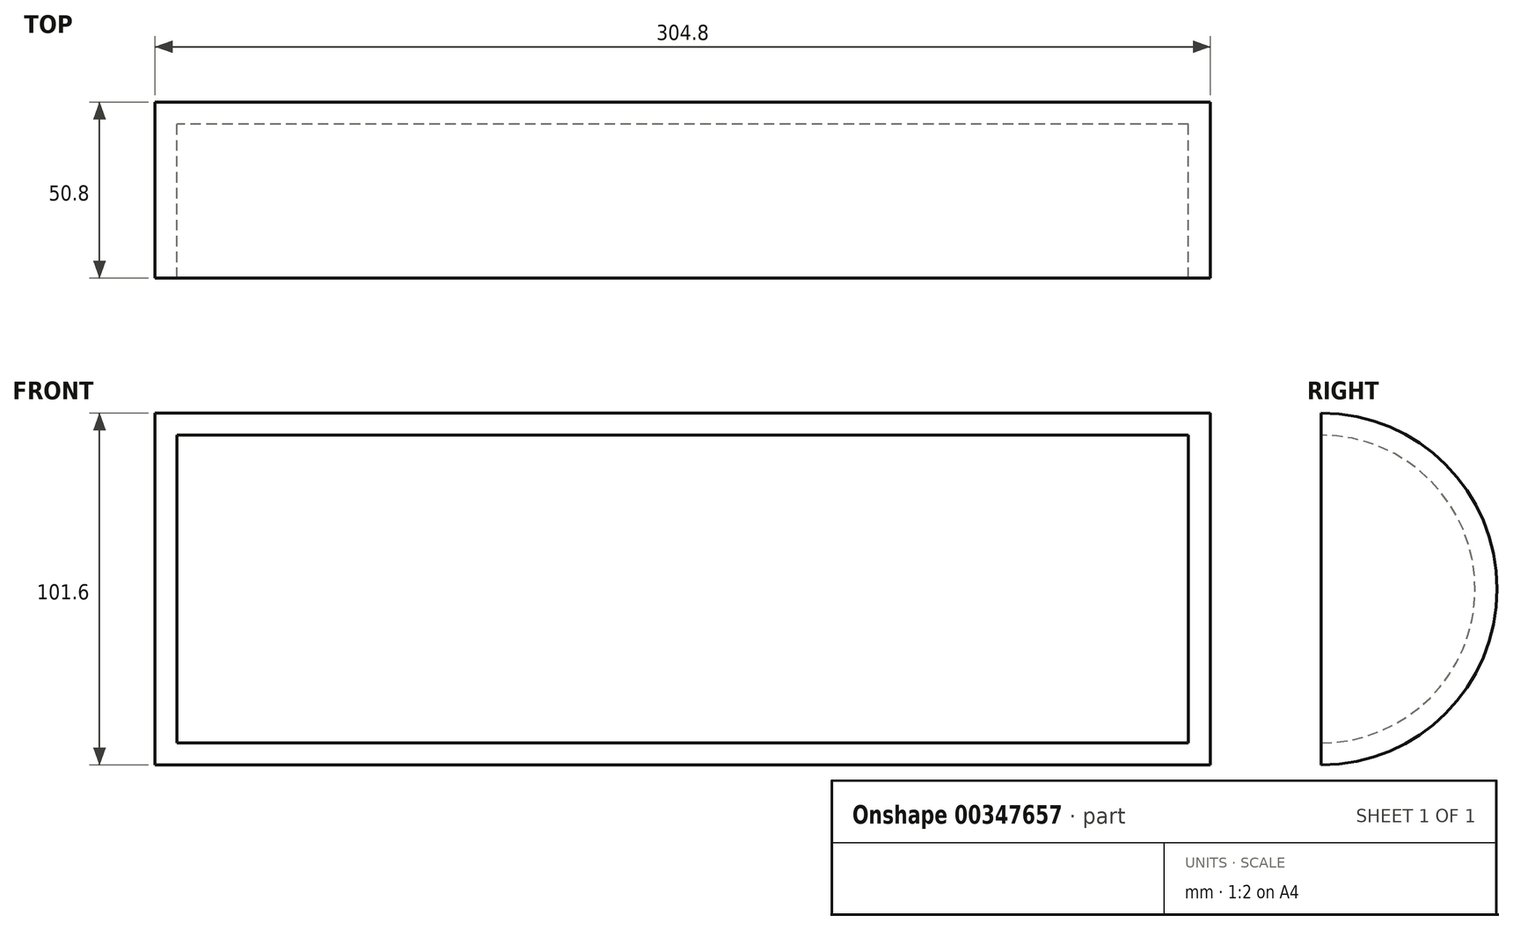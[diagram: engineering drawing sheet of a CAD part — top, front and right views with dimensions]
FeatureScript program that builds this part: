
annotation { "Feature Type Name" : "Feature", "Feature Type Description" : "" }
export const myFeature = defineFeature(function(context is Context, id is Id, definition is map)
    precondition{}
    {
        {
            var Q0;
            Q0=qCreatedBy(makeId("Right.planeOp"),FACE);
            var sketch = newSketch(context, id + "F0", { "sketchPlane" : qUnion([Q0])});
            skCircle(sketch, "E0", {"center": v(0, 0) * mm, "radius": 50.8 * mm});
            skLineSegment(sketch, "E1", {"start": v(0, 50.8) * mm, "end": v(0, -50.8) * mm});
            skSolve(sketch);
        }
        {
            var Q0;
            {var subQ0=sQuery(id+"F0.wireOp",EDGE,"E1");Q0=makeQuery(id+"F0.imprint","IMPRINT",FACE,{"disambiguationData":[TD([[makeQuery(id+"F0.imprint","IMPRINT",EDGE,{"derivedFrom":subQ0}),1.0]])]});}
            extrude(context, id + "F1", {"entities" : qUnion([Q0]), "depth" : 304.8 * mm, "hasSecondDirection" : true, "secondDirectionOppositeDirection" : true, "secondDirectionDepth" : 76.2 * mm, "symmetric" : true});
        }
        {
            var Q0;
            Q0=makeQuery(id+"F1.opExtrude","SWEPT_FACE",FACE,{"disambiguationData":[OSD([sQuery(id+"F0.wireOp",EDGE,"E1")])]});
            shell(context, id + "F2", {"entities" : qUnion([Q0]), "thickness" : 6.35 * mm});
        }
    });
